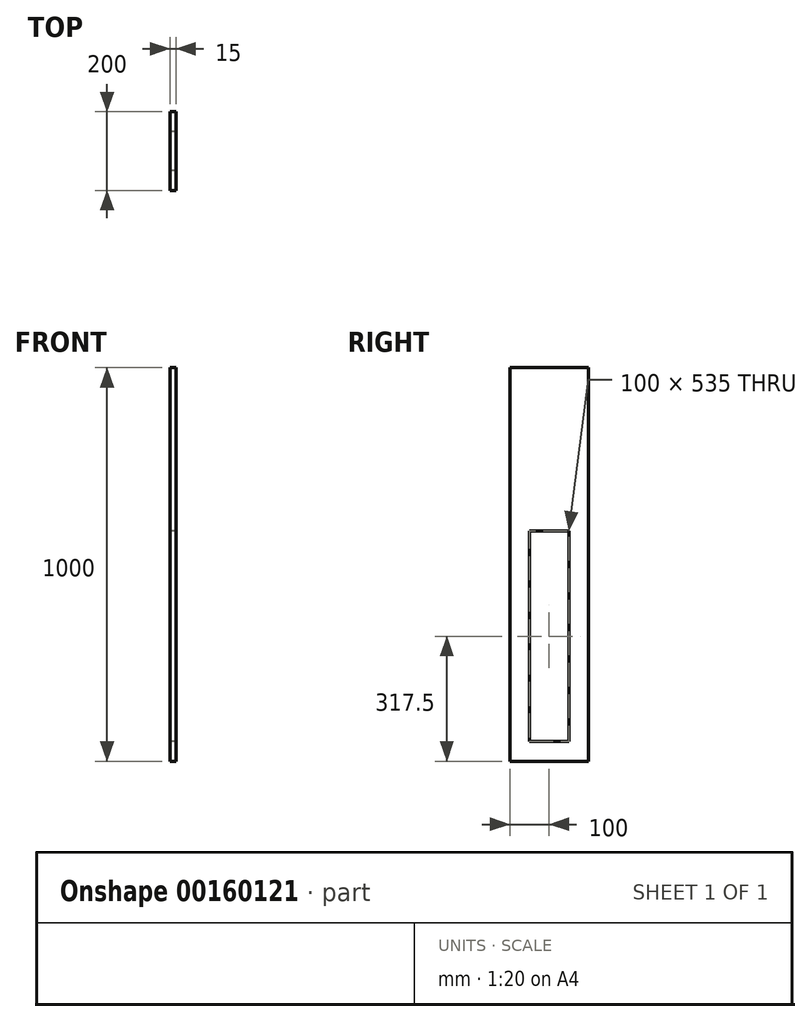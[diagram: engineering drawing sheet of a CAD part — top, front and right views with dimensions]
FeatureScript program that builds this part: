
annotation { "Feature Type Name" : "Feature", "Feature Type Description" : "" }
export const myFeature = defineFeature(function(context is Context, id is Id, definition is map)
    precondition{}
    {
        {
            var Q0;
            Q0=qCreatedBy(makeId("Right.planeOp"),FACE);
            var sketch = newSketch(context, id + "F0", { "sketchPlane" : qUnion([Q0])});
            skLineSegment(sketch, "E0.bottom", {"start": v(-297.08, 494.27) * mm, "end": v(-97.08, 494.27) * mm});
            skLineSegment(sketch, "E0.top", {"start": v(-297.08, -505.73) * mm, "end": v(-97.08, -505.73) * mm});
            skLineSegment(sketch, "E0.left", {"start": v(-297.08, 494.27) * mm, "end": v(-297.08, -505.73) * mm});
            skLineSegment(sketch, "E0.right", {"start": v(-97.08, 494.27) * mm, "end": v(-97.08, -505.73) * mm});
            skLineSegment(sketch, "E1.bottom", {"start": v(-247.08, 79.27) * mm, "end": v(-147.08, 79.27) * mm});
            skLineSegment(sketch, "E1.top", {"start": v(-247.08, -455.73) * mm, "end": v(-147.08, -455.73) * mm});
            skLineSegment(sketch, "E1.left", {"start": v(-247.08, 79.27) * mm, "end": v(-247.08, -455.73) * mm});
            skLineSegment(sketch, "E1.right", {"start": v(-147.08, 79.27) * mm, "end": v(-147.08, -455.73) * mm});
            skSolve(sketch);
        }
        {
            var Q0;
            Q0=makeQuery(id+"F0.imprint","IMPRINT",FACE,{"disambiguationData":[TD([[makeQuery(id+"F0.imprint","IMPRINT",EDGE,{"derivedFrom":sQuery(id+"F0.wireOp",EDGE,"E0.bottom")}),-1.0]])]});
            extrude(context, id + "F1", {"entities" : qUnion([Q0]), "depth" : 15 * mm});
        }
    });
